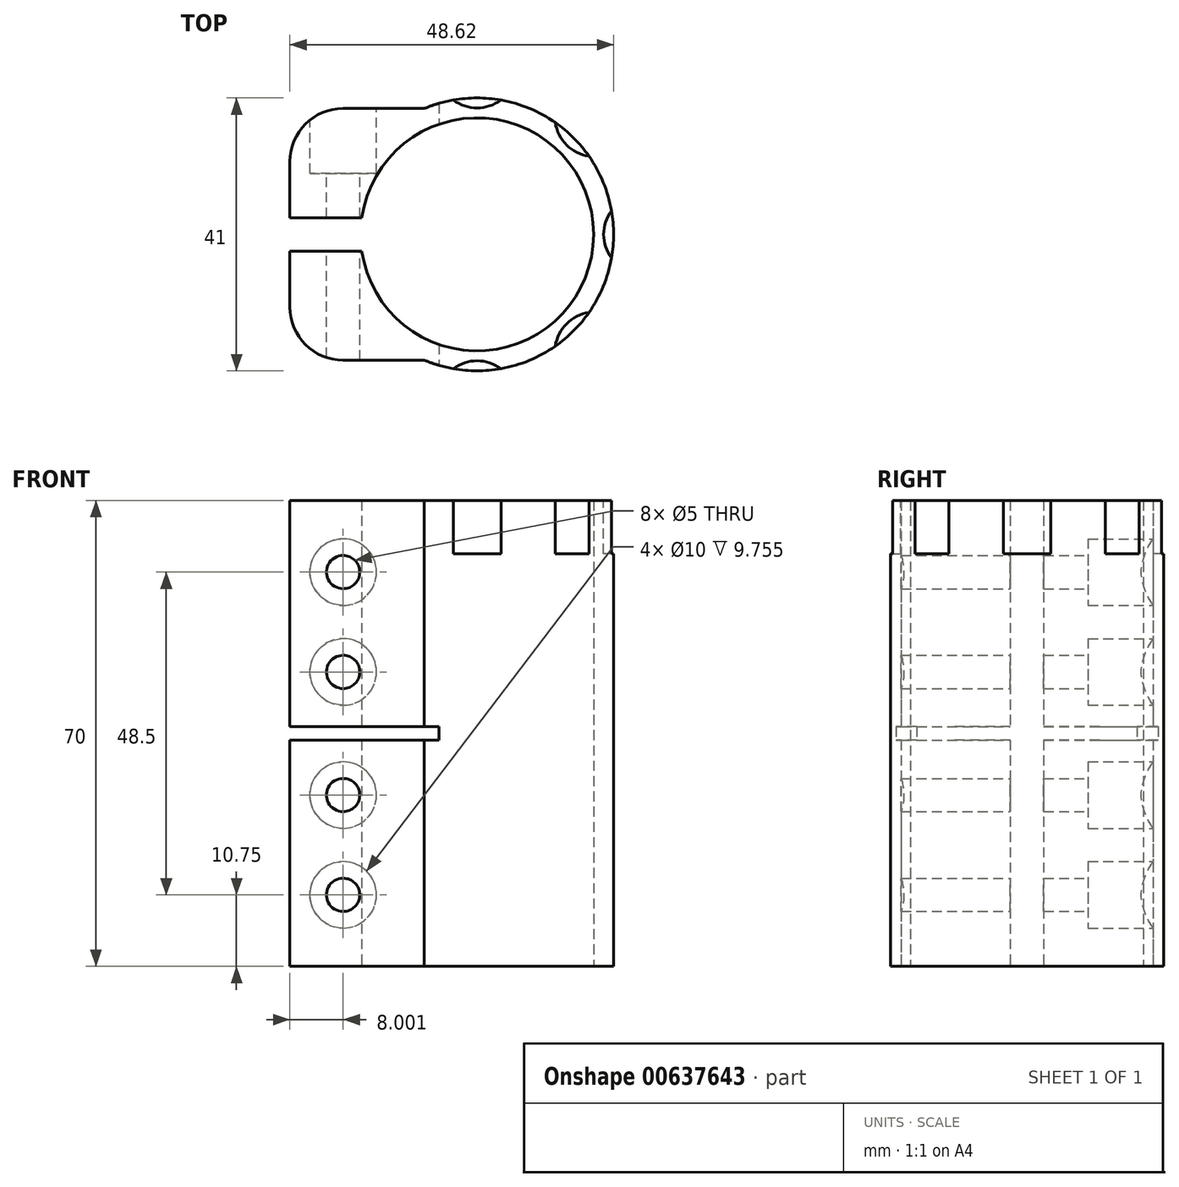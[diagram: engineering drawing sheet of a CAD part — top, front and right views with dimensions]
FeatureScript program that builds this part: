
annotation { "Feature Type Name" : "Feature", "Feature Type Description" : "" }
export const myFeature = defineFeature(function(context is Context, id is Id, definition is map)
    precondition{}
    {
        {
            var Q0;
            Q0=qCreatedBy(makeId("Top.planeOp"),FACE);
            var sketch = newSketch(context, id + "F0", { "sketchPlane" : qUnion([Q0])});
            skArc(sketch, "E0", {"start": v(-7.92, -18.9) * mm, "mid": v(20.5, 0) * mm, "end": v(-7.92, 18.9) * mm});
            skArc(sketch, "E1", {"start": v(-17.32, -2.5) * mm, "mid": v(17.5, 0) * mm, "end": v(-17.32, 2.5) * mm});
            skLineSegment(sketch, "E2", {"start": v(-7.92, 18.9) * mm, "end": v(-20.12, 18.9) * mm});
            skLineSegment(sketch, "E3", {"start": v(-28.12, 10.9) * mm, "end": v(-28.12, 2.5) * mm});
            skLineSegment(sketch, "E4", {"start": v(-28.12, 2.5) * mm, "end": v(-17.32, 2.5) * mm});
            skPoint(sketch, "E5.visualSharp", {"position": v(-28.12, 18.9) * mm});
            skArc(sketch, "E5.filletArc", {"start": v(-20.12, 18.9) * mm, "mid": v(-25.78, 16.57) * mm, "end": v(-28.12, 10.9) * mm});
            skLineSegment(sketch, "E6", {"start": v(0, 0) * mm, "end": v(41.3, 0) * mm, "construction": true});
            skLineSegment(sketch, "E7.MirrorCS", {"start": v(-28.12, -2.5) * mm, "end": v(-17.32, -2.5) * mm});
            skLineSegment(sketch, "E8.MirrorCS", {"start": v(-7.92, -18.9) * mm, "end": v(-20.12, -18.9) * mm});
            skLineSegment(sketch, "E9.MirrorCS", {"start": v(-28.12, -10.9) * mm, "end": v(-28.12, -2.5) * mm});
            skArc(sketch, "E10.MirrorCS", {"start": v(-20.12, -18.9) * mm, "mid": v(-25.78, -16.57) * mm, "end": v(-28.12, -10.9) * mm});
            skSolve(sketch);
        }
        {
            var Q0;
            Q0 = qSketchRegion(id + "F0", true);
            extrude(context, id + "F1", {"entities" : qUnion([Q0]), "endBound" : BoundingType.SYMMETRIC, "depth" : 70 * mm, "offsetDistance" : 25 * mm});
        }
        {
            var Q0;
            Q0=makeQuery(id+"F1.opExtrude","SWEPT_FACE",FACE,{"disambiguationData":[OSD([sQuery(id+"F0.wireOp",EDGE,"E2")])]});
            var sketch = newSketch(context, id + "F2", { "sketchPlane" : qUnion([Q0])});
            skPoint(sketch, "E11", {"position": v(20.12, -24.25) * mm});
            skPoint(sketch, "E12", {"position": v(20.12, -9.25) * mm});
            skPoint(sketch, "E13", {"position": v(20.12, 9.25) * mm});
            skPoint(sketch, "E14", {"position": v(20.12, 24.25) * mm});
            skSolve(sketch);
        }
        {
            var Q0;
            Q0=sQuery(id+"F2.wireOp",VERTEX,"E14");
            var Q1;
            Q1=sQuery(id+"F2.wireOp",VERTEX,"E13");
            var Q2;
            Q2=sQuery(id+"F2.wireOp",VERTEX,"E12");
            var Q3;
            Q3=sQuery(id+"F2.wireOp",VERTEX,"E11");
            var Q4;
            Q4=makeQuery(id+"F1.opExtrude","SWEPT_BODY",BODY,{"disambiguationData":[OSD([sQuery(id+"F0.wireOp",EDGE,"E0"),sQuery(id+"F0.wireOp",EDGE,"E1"),sQuery(id+"F0.wireOp",EDGE,"E2"),sQuery(id+"F0.wireOp",EDGE,"E3"),sQuery(id+"F0.wireOp",EDGE,"E4"),sQuery(id+"F0.wireOp",EDGE,"E5.filletArc"),sQuery(id+"F0.wireOp",EDGE,"E7.MirrorCS"),sQuery(id+"F0.wireOp",EDGE,"E8.MirrorCS"),sQuery(id+"F0.wireOp",EDGE,"E9.MirrorCS"),sQuery(id+"F0.wireOp",EDGE,"E10.MirrorCS")])]});
            hole(context, id + "F3", {"style" : HoleStyle.C_BORE, "endStyle" : HoleEndStyle.THROUGH, "holeDiameter" : 5 * mm, "cBoreDiameter" : 10 * mm, "cBoreDepth" : 8 * mm, "majorDiameter" : 5 * mm, "isTappedThrough" : true, "tappedDepth" : 12 * mm, "tapClearance" : 3, "locations" : qUnion([Q0, Q1, Q2, Q3]), "scope" : qUnion([Q4])});
        }
        {
            var Q0;
            Q0=qCreatedBy(makeId("Front.planeOp"),FACE);
            var sketch = newSketch(context, id + "F4", { "sketchPlane" : qUnion([Q0])});
            skLineSegment(sketch, "E15.bottom", {"start": v(-28.12, 1) * mm, "end": v(-5.72, 1) * mm});
            skLineSegment(sketch, "E15.top", {"start": v(-28.12, -1) * mm, "end": v(-5.72, -1) * mm});
            skLineSegment(sketch, "E15.left", {"start": v(-28.12, 1) * mm, "end": v(-28.12, -1) * mm});
            skLineSegment(sketch, "E15.right", {"start": v(-5.72, 1) * mm, "end": v(-5.72, -1) * mm});
            skSolve(sketch);
        }
        {
            var Q0;
            Q0 = qSketchRegion(id + "F4", true);
            extrude(context, id + "F5", {"entities" : qUnion([Q0]), "operationType" : NewBodyOperationType.REMOVE, "endBound" : BoundingType.SYMMETRIC, "oppositeDirection" : true, "depth" : 50 * mm, "offsetDistance" : 25 * mm});
        }
        {
            var Q0;
            Q0=makeQuery(id+"F1.opExtrude","CAP_FACE",FACE,{"disambiguationData":[OSD([sQuery(id+"F0.wireOp",EDGE,"E0"),sQuery(id+"F0.wireOp",EDGE,"E1"),sQuery(id+"F0.wireOp",EDGE,"E2"),sQuery(id+"F0.wireOp",EDGE,"E3"),sQuery(id+"F0.wireOp",EDGE,"E4"),sQuery(id+"F0.wireOp",EDGE,"E5.filletArc"),sQuery(id+"F0.wireOp",EDGE,"E7.MirrorCS"),sQuery(id+"F0.wireOp",EDGE,"E8.MirrorCS"),sQuery(id+"F0.wireOp",EDGE,"E9.MirrorCS"),sQuery(id+"F0.wireOp",EDGE,"E10.MirrorCS")])],"isStart":false});
            var sketch = newSketch(context, id + "F6", { "sketchPlane" : qUnion([Q0])});
            skCircle(sketch, "E16", {"center": v(0, -25) * mm, "radius": 6 * mm});
            skCircle(sketch, "E17.1.0", {"center": v(17.68, -17.68) * mm, "radius": 6 * mm});
            skCircle(sketch, "E17.2.0", {"center": v(25, 0) * mm, "radius": 6 * mm});
            skCircle(sketch, "E17.3.0", {"center": v(17.68, 17.68) * mm, "radius": 6 * mm});
            skCircle(sketch, "E17.4.0", {"center": v(0, 25) * mm, "radius": 6 * mm});
            skPoint(sketch, "E17.center", {"position": v(0, 0) * mm});
            skLineSegment(sketch, "E17.anchor1", {"start": v(0, 0) * mm, "end": v(0, -25) * mm, "construction": true});
            skLineSegment(sketch, "E17.anchor2", {"start": v(0, 0) * mm, "end": v(0, 25) * mm, "construction": true});
            skSolve(sketch);
        }
        {
            var Q0;
            Q0 = qSketchRegion(id + "F6", true);
            extrude(context, id + "F7", {"entities" : qUnion([Q0]), "operationType" : NewBodyOperationType.REMOVE, "oppositeDirection" : true, "depth" : 8 * mm, "offsetDistance" : 25 * mm});
        }
    });
